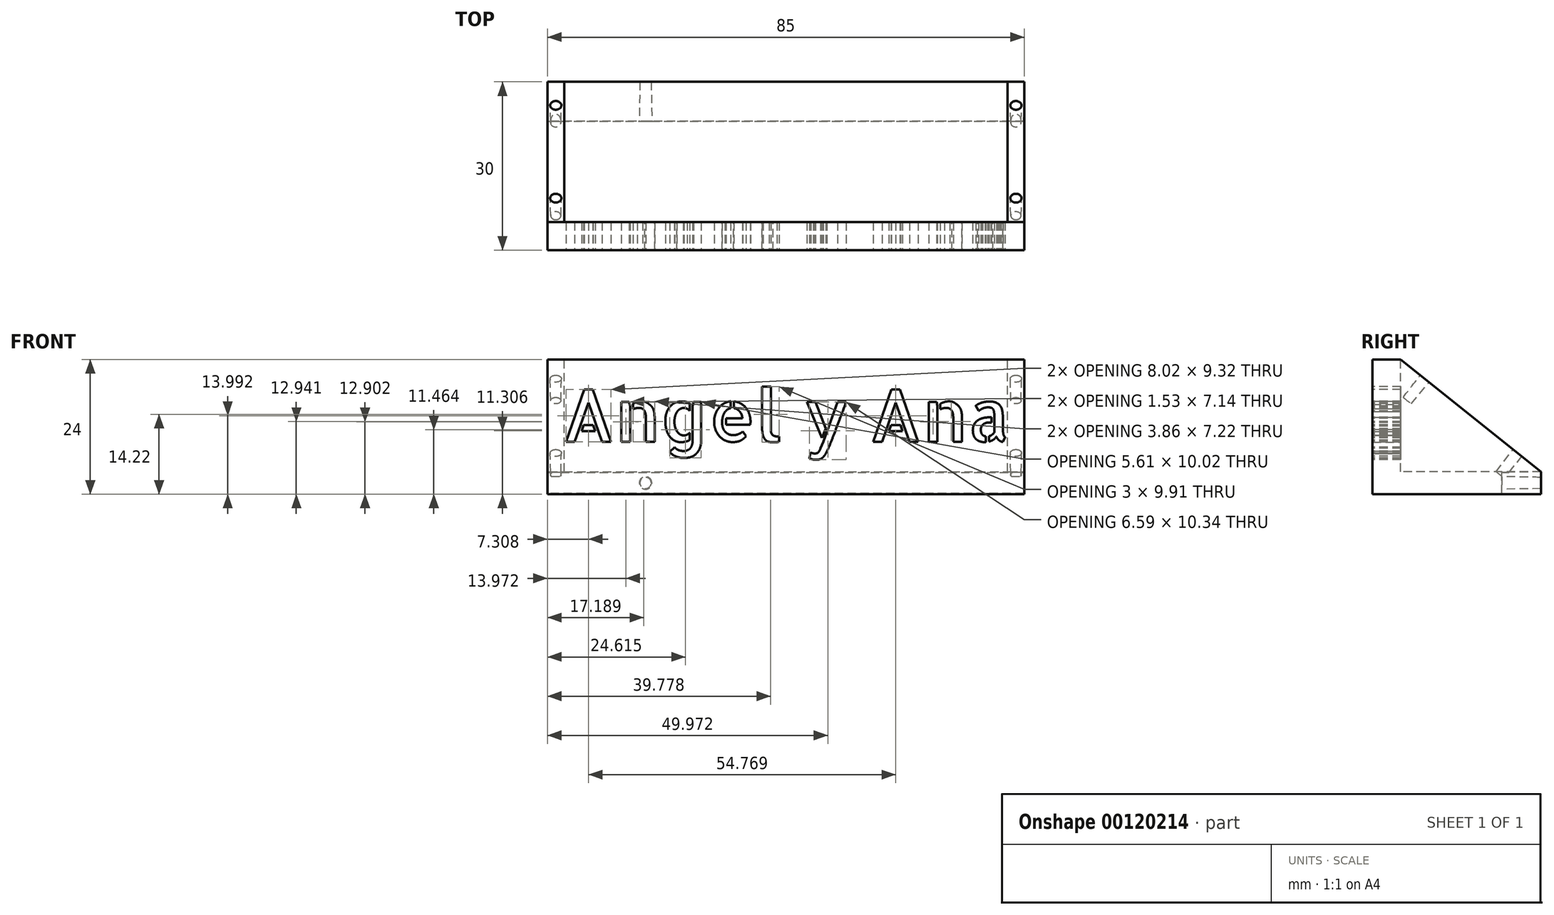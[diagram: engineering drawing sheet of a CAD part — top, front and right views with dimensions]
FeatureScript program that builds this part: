
annotation { "Feature Type Name" : "Feature", "Feature Type Description" : "" }
export const myFeature = defineFeature(function(context is Context, id is Id, definition is map)
    precondition{}
    {
        {
            var Q0;
            Q0=qCreatedBy(makeId("Front.planeOp"),FACE);
            var sketch = newSketch(context, id + "F0", { "sketchPlane" : qUnion([Q0])});
            skLineSegment(sketch, "E0.bottom", {"start": v(-2.5, -5.33) * mm, "end": v(82.5, -5.33) * mm});
            skLineSegment(sketch, "E0.top", {"start": v(-2.5, 14.67) * mm, "end": v(82.5, 14.67) * mm});
            skLineSegment(sketch, "E0.left", {"start": v(-2.5, -5.33) * mm, "end": v(-2.5, 14.67) * mm});
            skLineSegment(sketch, "E0.right", {"start": v(82.5, -5.33) * mm, "end": v(82.5, 14.67) * mm});
            skLineSegment(sketch, "E1", {"start": v(-2.5, 4.67) * mm, "end": v(82.5, 4.67) * mm, "construction": true});
            skLineSegment(sketch, "E2.bottom", {"start": v(80, 9.34) * mm, "end": v(0, 9.34) * mm, "construction": true});
            skLineSegment(sketch, "E2.top", {"start": v(80, 0) * mm, "end": v(0, 0) * mm, "construction": true});
            skLineSegment(sketch, "E2.left", {"start": v(80, 9.34) * mm, "end": v(80, 0) * mm, "construction": true});
            skLineSegment(sketch, "E2.right", {"start": v(0, 9.34) * mm, "end": v(0, 0) * mm, "construction": true});
            skPoint(sketch, "E2.middle", {"position": v(40, 4.67) * mm});
            skText(sketch, "E3", { "text": "Angel y Ana", "fontName": "AllertaStencil-Regular.ttf"});
            skLineSegment(sketch, "E4.top", {"start": v(-2.5, -9.33) * mm, "end": v(82.5, -9.33) * mm});
            skLineSegment(sketch, "E4.left", {"start": v(-2.5, -5.33) * mm, "end": v(-2.5, -9.33) * mm});
            skLineSegment(sketch, "E4.right", {"start": v(82.5, -5.33) * mm, "end": v(82.5, -9.33) * mm});
            const initialGuessF0  = {"E3": [0, 0, 1, 0, 0.00934]};
            skSetInitialGuess(sketch, initialGuessF0);
            skSolve(sketch);
        }
        {
            var Q0;
            Q0=makeQuery(id+"F0.imprint","IMPRINT",FACE,{"disambiguationData":[TD([[makeQuery(id+"F0.imprint","IMPRINT",EDGE,{"derivedFrom":sQuery(id+"F0.wireOp",EDGE,"E0.top")}),-1.0]])]});
            extrude(context, id + "F1", {"entities" : qUnion([Q0]), "oppositeDirection" : true, "depth" : 5 * mm});
        }
        {
            var Q0;
            Q0=makeQuery(id+"F0.imprint","IMPRINT",FACE,{"disambiguationData":[TD([[makeQuery(id+"F0.imprint","IMPRINT",EDGE,{"derivedFrom":sQuery(id+"F0.wireOp",EDGE,"E0.bottom")}),-1.0]])]});
            extrude(context, id + "F2", {"entities" : qUnion([Q0]), "operationType" : NewBodyOperationType.ADD, "oppositeDirection" : true, "depth" : 30 * mm});
        }
        {
            var Q0;
            Q0=makeQuery(id+"F2.boolean.opBoolean","MERGE",FACE,{"derivedFrom":[makeQuery(id+"F1.opExtrude","SWEPT_FACE",FACE,{"disambiguationData":[OSD([sQuery(id+"F0.wireOp",EDGE,"E0.right")])]}),makeQuery(id+"F2.opExtrude","SWEPT_FACE",FACE,{"disambiguationData":[OSD([sQuery(id+"F0.wireOp",EDGE,"E4.right")])]})]});
            var sketch = newSketch(context, id + "F3", { "sketchPlane" : qUnion([Q0])});
            skLineSegment(sketch, "E5", {"start": v(5, 14.67) * mm, "end": v(30, -5.33) * mm});
            skSolve(sketch);
        }
        {
            var Q0;
            Q0=makeQuery(id+"F2.boolean.opBoolean","MERGE",FACE,{"derivedFrom":[makeQuery(id+"F1.opExtrude","SWEPT_FACE",FACE,{"disambiguationData":[OSD([sQuery(id+"F0.wireOp",EDGE,"E0.left")])]}),makeQuery(id+"F2.opExtrude","SWEPT_FACE",FACE,{"disambiguationData":[OSD([sQuery(id+"F0.wireOp",EDGE,"E4.left")])]})]});
            var sketch = newSketch(context, id + "F4", { "sketchPlane" : qUnion([Q0])});
            skLineSegment(sketch, "E6", {"start": v(-30, -5.33) * mm, "end": v(-5, 14.67) * mm});
            skSolve(sketch);
        }
        {
            var Q0;
            Q0=makeQuery(id+"F4.imprint","IMPRINT",FACE,{"disambiguationData":[TD([[makeQuery(id+"F4.imprint","IMPRINT",EDGE,{"derivedFrom":sQuery(id+"F4.wireOp",EDGE,"E6")}),-1.0]])]});
            extrude(context, id + "F5", {"entities" : qUnion([Q0]), "operationType" : NewBodyOperationType.ADD, "oppositeDirection" : true, "depth" : 3 * mm});
        }
        {
            var Q0;
            Q0=makeQuery(id+"F3.imprint","IMPRINT",FACE,{"disambiguationData":[TD([[makeQuery(id+"F3.imprint","IMPRINT",EDGE,{"derivedFrom":sQuery(id+"F3.wireOp",EDGE,"E5")}),-1.0]])]});
            extrude(context, id + "F6", {"entities" : qUnion([Q0]), "operationType" : NewBodyOperationType.ADD, "oppositeDirection" : true, "depth" : 3 * mm});
        }
        {
            var Q0;
            Q0=makeQuery(id+"F6.opExtrude","SWEPT_FACE",FACE,{"disambiguationData":[OSD([sQuery(id+"F3.wireOp",EDGE,"E5")])]});
            var sketch = newSketch(context, id + "F7", { "sketchPlane" : qUnion([Q0])});
            skLineSegment(sketch, "E7", {"start": v(81, -5.26) * mm, "end": v(81, 26.75) * mm, "construction": true});
            skCircle(sketch, "E8", {"center": v(81, 0.2) * mm, "radius": 1 * mm});
            skCircle(sketch, "E9", {"center": v(81, 21.4) * mm, "radius": 1 * mm});
            skLineSegment(sketch, "E10", {"start": v(81, 0.2) * mm, "end": v(-3.76, 0.2) * mm, "construction": true});
            skLineSegment(sketch, "E11", {"start": v(81, 21.4) * mm, "end": v(-3.76, 21.4) * mm, "construction": true});
            skSolve(sketch);
        }
        {
            var Q0;
            Q0=makeQuery(id+"F5.opExtrude","SWEPT_FACE",FACE,{"disambiguationData":[OSD([sQuery(id+"F4.wireOp",EDGE,"E6")])]});
            var sketch = newSketch(context, id + "F8", { "sketchPlane" : qUnion([Q0])});
            skLineSegment(sketch, "E12", {"start": v(-1, -5.26) * mm, "end": v(-1, 26.75) * mm, "construction": true});
            skCircle(sketch, "E13", {"center": v(-1, 21.4) * mm, "radius": 1 * mm});
            skCircle(sketch, "E14", {"center": v(-1, 0.2) * mm, "radius": 1 * mm});
            skSolve(sketch);
        }
        {
            var Q0;
            Q0=makeQuery(id+"F1.opExtrude","SWEPT_FACE",FACE,{"disambiguationData":[OSD([sQuery(id+"F0.wireOp",EDGE,"E0.top")])]});
            var sketch = newSketch(context, id + "F9", { "sketchPlane" : qUnion([Q0])});
            skLineSegment(sketch, "E15", {"start": v(82.5, 2.5) * mm, "end": v(-2.5, 2.5) * mm, "construction": true});
            skCircle(sketch, "E16", {"center": v(40, 2.5) * mm, "radius": 1 * mm});
            skSolve(sketch);
        }
        {
            var Q0;
            Q0=makeQuery(id+"F2.opExtrude","CAP_FACE",FACE,{"disambiguationData":[OSD([sQuery(id+"F0.wireOp",EDGE,"E0.bottom"),sQuery(id+"F0.wireOp",EDGE,"E4.top"),sQuery(id+"F0.wireOp",EDGE,"E4.left"),sQuery(id+"F0.wireOp",EDGE,"E4.right")])],"isStart":false});
            var sketch = newSketch(context, id + "F10", { "sketchPlane" : qUnion([Q0])});
            skLineSegment(sketch, "E17", {"start": v(-40, -5.33) * mm, "end": v(-40, -9.33) * mm, "construction": true});
            skLineSegment(sketch, "E18", {"start": v(-40, -7.33) * mm, "end": v(-65, -7.33) * mm, "construction": true});
            skCircle(sketch, "E19", {"center": v(-65, -7.33) * mm, "radius": 1 * mm});
            skCircle(sketch, "E20.MirrorC", {"center": v(-15, -7.33) * mm, "radius": 1 * mm});
            skSolve(sketch);
        }
        {
            var Q0;
            Q0=makeQuery(id+"F10.imprint","IMPRINT",FACE,{"disambiguationData":[TD([[makeQuery(id+"F10.imprint","IMPRINT",EDGE,{"derivedFrom":sQuery(id+"F10.wireOp",EDGE,"E19")}),1.0]])]});
            var Q1;
            Q1=makeQuery(id+"F10.imprint","IMPRINT",FACE,{"disambiguationData":[TD([[makeQuery(id+"F10.imprint","IMPRINT",EDGE,{"derivedFrom":sQuery(id+"F10.wireOp",EDGE,"E20.MirrorC")}),-1.0]])]});
            extrude(context, id + "F11", {"entities" : qUnion([Q0, Q1]), "operationType" : NewBodyOperationType.REMOVE, "oppositeDirection" : true, "depth" : 7 * mm, "hasDraft" : true, "draftAngle" : 1 * degree, "draftPullDirection" : true});
        }
        {
            var Q0;
            Q0=makeQuery(id+"F7.imprint","IMPRINT",FACE,{"disambiguationData":[TD([[makeQuery(id+"F7.imprint","IMPRINT",EDGE,{"derivedFrom":sQuery(id+"F7.wireOp",EDGE,"E8")}),1.0]])]});
            var Q1;
            Q1=makeQuery(id+"F8.imprint","IMPRINT",FACE,{"disambiguationData":[TD([[makeQuery(id+"F8.imprint","IMPRINT",EDGE,{"derivedFrom":sQuery(id+"F8.wireOp",EDGE,"E14")}),1.0]])]});
            var Q2;
            Q2=makeQuery(id+"F8.imprint","IMPRINT",FACE,{"disambiguationData":[TD([[makeQuery(id+"F8.imprint","IMPRINT",EDGE,{"derivedFrom":sQuery(id+"F8.wireOp",EDGE,"E13")}),1.0]])]});
            var Q3;
            Q3=makeQuery(id+"F7.imprint","IMPRINT",FACE,{"disambiguationData":[TD([[makeQuery(id+"F7.imprint","IMPRINT",EDGE,{"derivedFrom":sQuery(id+"F7.wireOp",EDGE,"E9")}),1.0]])]});
            extrude(context, id + "F12", {"entities" : qUnion([Q0, Q1, Q2, Q3]), "operationType" : NewBodyOperationType.REMOVE, "oppositeDirection" : true, "depth" : 5 * mm, "hasDraft" : true, "draftAngle" : 1 * degree, "draftPullDirection" : true});
        }
        {
            var Q0;
            Q0=makeQuery(id+"F9.imprint","IMPRINT",FACE,{"disambiguationData":[TD([[makeQuery(id+"F9.imprint","IMPRINT",EDGE,{"derivedFrom":sQuery(id+"F9.wireOp",EDGE,"E16")}),1.0]])]});
            extrude(context, id + "F13", {"entities" : qUnion([Q0]), "operationType" : NewBodyOperationType.REMOVE, "depth" : 8 * mm, "hasDraft" : true, "draftAngle" : 1 * degree, "draftPullDirection" : true});
        }
    });
